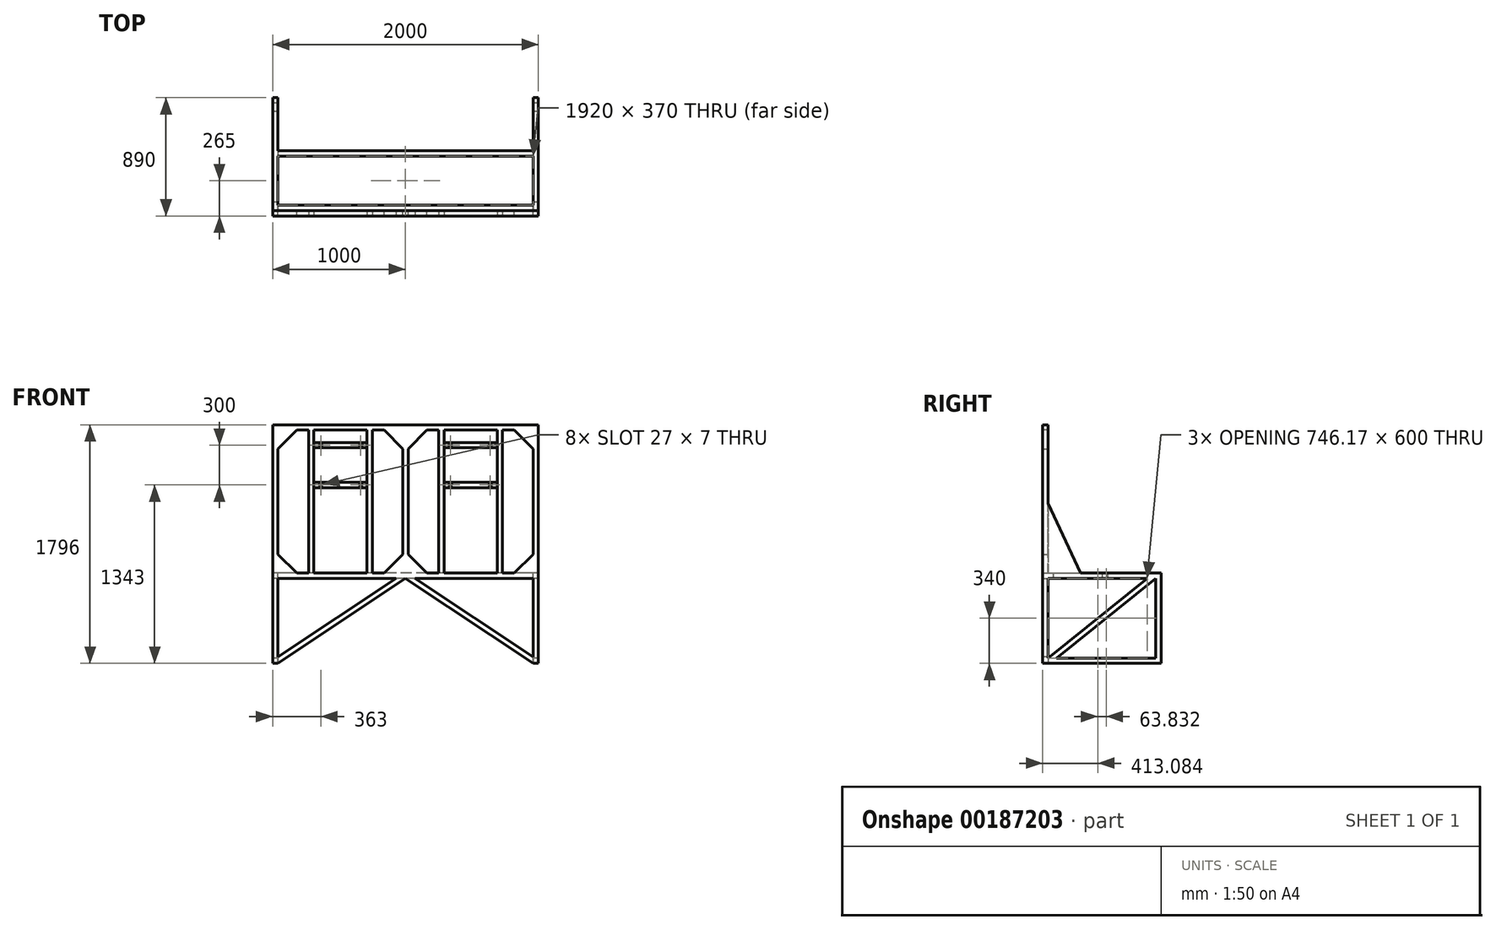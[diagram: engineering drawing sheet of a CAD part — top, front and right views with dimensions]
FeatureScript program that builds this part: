
annotation { "Feature Type Name" : "Feature", "Feature Type Description" : "" }
export const myFeature = defineFeature(function(context is Context, id is Id, definition is map)
    precondition{}
    {
        {
            var Q0;
            Q0=qCreatedBy(makeId("Front.planeOp"),FACE);
            var sketch = newSketch(context, id + "F0", { "sketchPlane" : qUnion([Q0])});
            skLineSegment(sketch, "E0.bottom", {"start": v(1000, -898) * mm, "end": v(-1000, -898) * mm});
            skLineSegment(sketch, "E0.top", {"start": v(1000, 898) * mm, "end": v(-1000, 898) * mm});
            skLineSegment(sketch, "E0.left", {"start": v(1000, -898) * mm, "end": v(1000, 898) * mm});
            skLineSegment(sketch, "E0.right", {"start": v(-1000, -898) * mm, "end": v(-1000, 898) * mm});
            skPoint(sketch, "E0.middle", {"position": v(0, 0) * mm});
            skSolve(sketch);
        }
        {
            var Q0;
            Q0 = qSketchRegion(id + "F0", true);
            extrude(context, id + "F1", {"entities" : qUnion([Q0]), "depth" : 40 * mm});
        }
        {
            var Q0;
            Q0=makeQuery(id+"F1.opExtrude","CAP_FACE",FACE,{"disambiguationData":[OSD([sQuery(id+"F0.wireOp",EDGE,"E0.bottom"),sQuery(id+"F0.wireOp",EDGE,"E0.top"),sQuery(id+"F0.wireOp",EDGE,"E0.left"),sQuery(id+"F0.wireOp",EDGE,"E0.right")])],"isStart":true});
            var sketch = newSketch(context, id + "F2", { "sketchPlane" : qUnion([Q0])});
            skLineSegment(sketch, "E1.bottom", {"start": v(-1000, -218) * mm, "end": v(1000, -218) * mm});
            skLineSegment(sketch, "E1.top", {"start": v(-1000, -898) * mm, "end": v(1000, -898) * mm});
            skLineSegment(sketch, "E1.left", {"start": v(1000, -218) * mm, "end": v(1000, -898) * mm});
            skLineSegment(sketch, "E1.right", {"start": v(-1000, -218) * mm, "end": v(-1000, -898) * mm});
            skSolve(sketch);
        }
        {
            var Q0;
            Q0 = qSketchRegion(id + "F2", true);
            extrude(context, id + "F3", {"entities" : qUnion([Q0]), "operationType" : NewBodyOperationType.ADD, "depth" : 850 * mm});
        }
        {
            var Q0;
            Q0=makeQuery(id+"F1.opExtrude","CAP_FACE",FACE,{"disambiguationData":[OSD([sQuery(id+"F0.wireOp",EDGE,"E0.bottom"),sQuery(id+"F0.wireOp",EDGE,"E0.top"),sQuery(id+"F0.wireOp",EDGE,"E0.left"),sQuery(id+"F0.wireOp",EDGE,"E0.right")])],"isStart":true});
            var sketch = newSketch(context, id + "F4", { "sketchPlane" : qUnion([Q0])});
            skLineSegment(sketch, "E2", {"start": v(0, 898) * mm, "end": v(0, -898) * mm, "construction": true});
            skLineSegment(sketch, "E3.bottom", {"start": v(960, -898) * mm, "end": v(-960, -898) * mm});
            skLineSegment(sketch, "E3.top", {"start": v(960, -258) * mm, "end": v(-960, -258) * mm});
            skLineSegment(sketch, "E3.left", {"start": v(-960, -898) * mm, "end": v(-960, -258) * mm});
            skLineSegment(sketch, "E3.right", {"start": v(960, -898) * mm, "end": v(960, -258) * mm});
            skPoint(sketch, "E3.middle", {"position": v(0, -578) * mm});
            skLineSegment(sketch, "E4", {"start": v(-20, -76.58) * mm, "end": v(-20, 716.58) * mm});
            skLineSegment(sketch, "E5.MirrorCS", {"start": v(-960, 716.58) * mm, "end": v(-960, -76.58) * mm});
            skLineSegment(sketch, "E6.MirrorCS", {"start": v(-960, 716.58) * mm, "end": v(-818.58, 858) * mm});
            skLineSegment(sketch, "E7", {"start": v(-818.58, 858) * mm, "end": v(-161.42, 858) * mm});
            skLineSegment(sketch, "E8", {"start": v(-161.42, 858) * mm, "end": v(-20, 716.58) * mm});
            skLineSegment(sketch, "E9.MirrorCS", {"start": v(20, -76.58) * mm, "end": v(20, 716.58) * mm});
            skLineSegment(sketch, "E10.MirrorCS", {"start": v(960, 716.58) * mm, "end": v(960, -76.58) * mm});
            skLineSegment(sketch, "E11.MirrorCS", {"start": v(960, 716.58) * mm, "end": v(818.58, 858) * mm});
            skLineSegment(sketch, "E12.MirrorCS", {"start": v(818.58, 858) * mm, "end": v(161.42, 858) * mm});
            skLineSegment(sketch, "E13.MirrorCS", {"start": v(161.42, 858) * mm, "end": v(20, 716.58) * mm});
            skLineSegment(sketch, "E14", {"start": v(960, 858) * mm, "end": v(960, 773.15) * mm, "construction": true});
            skLineSegment(sketch, "E15", {"start": v(960, 773.15) * mm, "end": v(875.15, 858) * mm, "construction": true});
            skLineSegment(sketch, "E16", {"start": v(875.15, 858) * mm, "end": v(960, 858) * mm, "construction": true});
            skLineSegment(sketch, "E17", {"start": v(818.58, 858) * mm, "end": v(831.56, 858) * mm, "construction": true});
            skPoint(sketch, "E17.endSnap0", {"position": v(917.57, 858) * mm});
            skLineSegment(sketch, "E18", {"start": v(960, 716.58) * mm, "end": v(960, 745.8) * mm, "construction": true});
            skLineSegment(sketch, "E19", {"start": v(490, 858) * mm, "end": v(490, 680.23) * mm, "construction": true});
            skPoint(sketch, "E19.endSnap0", {"position": v(490, 858) * mm});
            skLineSegment(sketch, "E20.MirrorCS", {"start": v(20, 773.15) * mm, "end": v(104.85, 858) * mm, "construction": true});
            skLineSegment(sketch, "E21.MirrorCS", {"start": v(104.85, 858) * mm, "end": v(20, 858) * mm, "construction": true});
            skPoint(sketch, "E22", {"position": v(960, 815.57) * mm});
            skLineSegment(sketch, "E23.MirrorCS", {"start": v(20, 858) * mm, "end": v(20, 773.15) * mm, "construction": true});
            skLineSegment(sketch, "E24.MirrorCS", {"start": v(-20, 773.15) * mm, "end": v(-104.85, 858) * mm, "construction": true});
            skLineSegment(sketch, "E25.MirrorCS", {"start": v(-20, 858) * mm, "end": v(-20, 773.15) * mm, "construction": true});
            skLineSegment(sketch, "E26.MirrorCS", {"start": v(-104.85, 858) * mm, "end": v(-20, 858) * mm, "construction": true});
            skLineSegment(sketch, "E27.MirrorCS", {"start": v(-960, 773.15) * mm, "end": v(-875.15, 858) * mm, "construction": true});
            skLineSegment(sketch, "E28.MirrorCS", {"start": v(-875.15, 858) * mm, "end": v(-960, 858) * mm, "construction": true});
            skLineSegment(sketch, "E29.MirrorCS", {"start": v(-960, 858) * mm, "end": v(-960, 773.15) * mm, "construction": true});
            skLineSegment(sketch, "E30", {"start": v(-960, -76.58) * mm, "end": v(-818.58, -218) * mm});
            skLineSegment(sketch, "E31", {"start": v(-818.58, -218) * mm, "end": v(-161.42, -218) * mm});
            skLineSegment(sketch, "E32", {"start": v(-161.42, -218) * mm, "end": v(-20, -76.58) * mm});
            skLineSegment(sketch, "E33.MirrorCS", {"start": v(161.42, -218) * mm, "end": v(20, -76.58) * mm});
            skLineSegment(sketch, "E34.MirrorCS", {"start": v(818.58, -218) * mm, "end": v(161.42, -218) * mm});
            skLineSegment(sketch, "E35.MirrorCS", {"start": v(960, -76.58) * mm, "end": v(818.58, -218) * mm});
            skPoint(sketch, "E36.0", {"position": v(1000, -218) * mm});
            skLineSegment(sketch, "E37", {"start": v(1000, -218) * mm, "end": v(818.58, -218) * mm, "construction": true});
            skSolve(sketch);
        }
        {
            var Q0;
            Q0 = qSketchRegion(id + "F4", true);
            extrude(context, id + "F5", {"entities" : qUnion([Q0]), "operationType" : NewBodyOperationType.REMOVE, "endBound" : BoundingType.THROUGH_ALL, "oppositeDirection" : true, "depth" : 25 * mm, "hasSecondDirection" : true, "secondDirectionBound" : SecondDirectionBoundingType.THROUGH_ALL, "secondDirectionOppositeDirection" : false, "secondDirectionDepth" : 25 * mm});
        }
        {
            var Q0;
            Q0=makeQuery(id+"F3.boolean.opBoolean","MERGE",FACE,{"derivedFrom":[makeQuery(id+"F1.opExtrude","SWEPT_FACE",FACE,{"disambiguationData":[OSD([sQuery(id+"F0.wireOp",EDGE,"E0.right")])]}),makeQuery(id+"F3.opExtrude","SWEPT_FACE",FACE,{"disambiguationData":[OSD([sQuery(id+"F2.wireOp",EDGE,"E1.left")])]})]});
            var sketch = newSketch(context, id + "F6", { "sketchPlane" : qUnion([Q0])});
            skLineSegment(sketch, "E38", {"start": v(-810, -258) * mm, "end": v(-810, -858) * mm});
            skLineSegment(sketch, "E39", {"start": v(-810, -858) * mm, "end": v(-63.83, -858) * mm});
            skLineSegment(sketch, "E40", {"start": v(-810, -258) * mm, "end": v(-63.83, -858) * mm});
            skLineSegment(sketch, "E41", {"start": v(0, -258) * mm, "end": v(0, -858) * mm});
            skLineSegment(sketch, "E42", {"start": v(0, -258) * mm, "end": v(-746.17, -258) * mm});
            skLineSegment(sketch, "E43", {"start": v(-746.17, -258) * mm, "end": v(0, -858) * mm});
            skSolve(sketch);
        }
        {
            var Q0;
            Q0 = qSketchRegion(id + "F6", true);
            extrude(context, id + "F7", {"entities" : qUnion([Q0]), "operationType" : NewBodyOperationType.REMOVE, "endBound" : BoundingType.THROUGH_ALL, "oppositeDirection" : true, "depth" : 25 * mm});
        }
        {
            var Q0;
            Q0=makeQuery(id+"F5.boolean.opBoolean","MERGE",FACE,{"derivedFrom":[makeQuery(id+"F3.opExtrude","SWEPT_FACE",FACE,{"disambiguationData":[OSD([sQuery(id+"F2.wireOp",EDGE,"E1.bottom")])]}),makeQuery(id+"F5.opExtrude","SWEPT_FACE",FACE,{"disambiguationData":[OSD([sQuery(id+"F4.wireOp",EDGE,"LeFSMORJ-KBJo-bJ4F-I0GN-BgiXlnm71I2b")])]}),makeQuery(id+"F5.opExtrude","SWEPT_FACE",FACE,{"disambiguationData":[OSD([sQuery(id+"F4.wireOp",EDGE,"b5f1aef8-d078-427e-881c-455c319d67770.MirrorCS")])]})]});
            var sketch = newSketch(context, id + "F8", { "sketchPlane" : qUnion([Q0])});
            skLineSegment(sketch, "E44", {"start": v(0, 900) * mm, "end": v(0, 210.95) * mm, "construction": true});
            skPoint(sketch, "E44.endSnap0", {"position": v(0, 984.2) * mm});
            skLineSegment(sketch, "E45.bottom", {"start": v(960, 450) * mm, "end": v(-960, 450) * mm});
            skLineSegment(sketch, "E45.top", {"start": v(960, 850) * mm, "end": v(-960, 850) * mm});
            skLineSegment(sketch, "E45.left", {"start": v(960, 450) * mm, "end": v(960, 850) * mm});
            skLineSegment(sketch, "E45.right", {"start": v(-960, 450) * mm, "end": v(-960, 850) * mm});
            skPoint(sketch, "E45.middle", {"position": v(0, 650) * mm});
            skLineSegment(sketch, "E46.bottom", {"start": v(960, 40) * mm, "end": v(-960, 40) * mm});
            skLineSegment(sketch, "E46.top", {"start": v(960, 410) * mm, "end": v(-960, 410) * mm});
            skLineSegment(sketch, "E46.left", {"start": v(960, 40) * mm, "end": v(960, 410) * mm});
            skLineSegment(sketch, "E46.right", {"start": v(-960, 40) * mm, "end": v(-960, 410) * mm});
            skPoint(sketch, "E46.middle", {"position": v(0, 225) * mm});
            skSolve(sketch);
        }
        {
            var Q0;
            Q0 = qSketchRegion(id + "F8", true);
            extrude(context, id + "F9", {"entities" : qUnion([Q0]), "operationType" : NewBodyOperationType.REMOVE, "endBound" : BoundingType.THROUGH_ALL, "oppositeDirection" : true, "depth" : 25 * mm});
        }
        {
            var Q0;
            Q0=makeQuery(id+"F1.opExtrude","CAP_FACE",FACE,{"disambiguationData":[OSD([sQuery(id+"F0.wireOp",EDGE,"E0.bottom"),sQuery(id+"F0.wireOp",EDGE,"E0.top"),sQuery(id+"F0.wireOp",EDGE,"E0.left"),sQuery(id+"F0.wireOp",EDGE,"E0.right")])],"isStart":false});
            var sketch = newSketch(context, id + "F10", { "sketchPlane" : qUnion([Q0])});
            skLineSegment(sketch, "E47", {"start": v(0, -258) * mm, "end": v(0, -518.97) * mm, "construction": true});
            skPoint(sketch, "E47.endSnap0", {"position": v(0, -258) * mm});
            skLineSegment(sketch, "E48", {"start": v(0, -258) * mm, "end": v(-960, -898) * mm});
            skLineSegment(sketch, "E49", {"start": v(-72.11, -258) * mm, "end": v(-960, -849.93) * mm});
            skLineSegment(sketch, "E50.MirrorCS", {"start": v(0, -258) * mm, "end": v(960, -898) * mm});
            skLineSegment(sketch, "E51.MirrorCS", {"start": v(72.11, -258) * mm, "end": v(960, -849.93) * mm});
            skLineSegment(sketch, "E52", {"start": v(0, -258) * mm, "end": v(-72.11, -258) * mm});
            skLineSegment(sketch, "E53", {"start": v(-960, -849.93) * mm, "end": v(-960, -898) * mm});
            skLineSegment(sketch, "E54.MirrorCS", {"start": v(960, -849.93) * mm, "end": v(960, -898) * mm});
            skLineSegment(sketch, "E55.MirrorCS", {"start": v(0, -258) * mm, "end": v(72.11, -258) * mm});
            skSolve(sketch);
        }
        {
            var Q0;
            Q0 = qSketchRegion(id + "F10", true);
            extrude(context, id + "F11", {"entities" : qUnion([Q0]), "operationType" : NewBodyOperationType.ADD, "oppositeDirection" : true, "depth" : 40 * mm});
        }
        {
            var Q0;
            Q0=makeQuery(id+"FoXpTRKPhEw7DUg_2.boolean.opBoolean","MERGE",FACE,{"derivedFrom":[makeQuery(id+"FZGJI4E4mUlCNrQ_1.boolean.opBoolean","MERGE",FACE,{"derivedFrom":[makeQuery(id+"F11.boolean.opBoolean","MERGE",FACE,{"derivedFrom":[makeQuery(id+"F1.opExtrude","CAP_FACE",FACE,{"disambiguationData":[OSD([sQuery(id+"F0.wireOp",EDGE,"E0.bottom"),sQuery(id+"F0.wireOp",EDGE,"E0.top"),sQuery(id+"F0.wireOp",EDGE,"E0.left"),sQuery(id+"F0.wireOp",EDGE,"E0.right")])],"isStart":false}),makeQuery(id+"F11.opExtrude","CAP_FACE",FACE,{"disambiguationData":[OSD([sQuery(id+"F10.wireOp",EDGE,"E48"),sQuery(id+"F10.wireOp",EDGE,"E49"),sQuery(id+"F10.wireOp",EDGE,"E52"),sQuery(id+"F10.wireOp",EDGE,"E53")])],"isStart":true}),makeQuery(id+"F11.opExtrude","CAP_FACE",FACE,{"disambiguationData":[OSD([sQuery(id+"F10.wireOp",EDGE,"E50.MirrorCS"),sQuery(id+"F10.wireOp",EDGE,"E51.MirrorCS"),sQuery(id+"F10.wireOp",EDGE,"E54.MirrorCS"),sQuery(id+"F10.wireOp",EDGE,"E55.MirrorCS")])],"isStart":true})]}),makeQuery(id+"FZGJI4E4mUlCNrQ_1.opExtrude","SWEPT_FACE",FACE,{"disambiguationData":[OSD([sQuery(id+"F2cN5tidunm1KXO_1.wireOp",EDGE,"B6aVEywH-Fo3N-waAX-fN73-OkDphfYnpIfc")])]})]}),makeQuery(id+"FoXpTRKPhEw7DUg_2.opExtrude","SWEPT_FACE",FACE,{"disambiguationData":[OSD([sQuery(id+"FMkWsH3aPkv592B_2.wireOp",EDGE,"YWnj1jYQ-A1Ux-tJnZ-8Nos-uWhglmEcxNfV")])]})]});
            var sketch = newSketch(context, id + "F12", { "sketchPlane" : qUnion([Q0])});
            skLineSegment(sketch, "E56.bottom", {"start": v(-730, 858) * mm, "end": v(-690, 858) * mm});
            skLineSegment(sketch, "E56.top", {"start": v(-730, -218) * mm, "end": v(-690, -218) * mm});
            skLineSegment(sketch, "E56.left", {"start": v(-730, 858) * mm, "end": v(-730, -218) * mm});
            skLineSegment(sketch, "E56.right", {"start": v(-690, 858) * mm, "end": v(-690, -218) * mm});
            skLineSegment(sketch, "E57", {"start": v(-490, 858) * mm, "end": v(-490, -218) * mm, "construction": true});
            skLineSegment(sketch, "E58.MirrorCS", {"start": v(-290, 858) * mm, "end": v(-290, -218) * mm});
            skLineSegment(sketch, "E59.MirrorCS", {"start": v(-250, 858) * mm, "end": v(-250, -218) * mm});
            skLineSegment(sketch, "E60.MirrorCS", {"start": v(-250, 858) * mm, "end": v(-290, 858) * mm});
            skLineSegment(sketch, "E61.MirrorCS", {"start": v(-250, -218) * mm, "end": v(-290, -218) * mm});
            skLineSegment(sketch, "E62", {"start": v(0, 898) * mm, "end": v(0, -218) * mm, "construction": true});
            skLineSegment(sketch, "E63.MirrorCS", {"start": v(250, 858) * mm, "end": v(250, -218) * mm});
            skLineSegment(sketch, "E64.MirrorCS", {"start": v(290, 858) * mm, "end": v(290, -218) * mm});
            skLineSegment(sketch, "E65.MirrorCS", {"start": v(690, 858) * mm, "end": v(690, -218) * mm});
            skLineSegment(sketch, "E66.MirrorCS", {"start": v(730, 858) * mm, "end": v(730, -218) * mm});
            skLineSegment(sketch, "E67.MirrorCS", {"start": v(730, -218) * mm, "end": v(690, -218) * mm});
            skLineSegment(sketch, "E68.MirrorCS", {"start": v(250, -218) * mm, "end": v(290, -218) * mm});
            skLineSegment(sketch, "E69.MirrorCS", {"start": v(250, 858) * mm, "end": v(290, 858) * mm});
            skLineSegment(sketch, "E70.MirrorCS", {"start": v(730, 858) * mm, "end": v(690, 858) * mm});
            skLineSegment(sketch, "E71", {"start": v(-161.42, -218) * mm, "end": v(161.42, -218) * mm, "construction": true});
            skSolve(sketch);
        }
        {
            var Q0;
            Q0 = qSketchRegion(id + "F12", true);
            extrude(context, id + "F13", {"entities" : qUnion([Q0]), "operationType" : NewBodyOperationType.ADD, "oppositeDirection" : true, "depth" : 40 * mm});
        }
        {
            var Q0;
            Q0=makeQuery(id+"F13.boolean.opBoolean","MERGE",FACE,{"derivedFrom":[makeQuery(id+"F1.opExtrude","CAP_FACE",FACE,{"disambiguationData":[OSD([sQuery(id+"F0.wireOp",EDGE,"E0.bottom"),sQuery(id+"F0.wireOp",EDGE,"E0.top"),sQuery(id+"F0.wireOp",EDGE,"E0.left"),sQuery(id+"F0.wireOp",EDGE,"E0.right")])],"isStart":true}),makeQuery(id+"F13.opExtrude","CAP_FACE",FACE,{"disambiguationData":[OSD([sQuery(id+"F12.wireOp",EDGE,"E56.bottom"),sQuery(id+"F12.wireOp",EDGE,"E56.top"),sQuery(id+"F12.wireOp",EDGE,"E56.left"),sQuery(id+"F12.wireOp",EDGE,"E56.right")])],"isStart":false}),makeQuery(id+"F13.opExtrude","CAP_FACE",FACE,{"disambiguationData":[OSD([sQuery(id+"F12.wireOp",EDGE,"E58.MirrorCS"),sQuery(id+"F12.wireOp",EDGE,"E59.MirrorCS"),sQuery(id+"F12.wireOp",EDGE,"E60.MirrorCS"),sQuery(id+"F12.wireOp",EDGE,"E61.MirrorCS")])],"isStart":false})]});
            var sketch = newSketch(context, id + "F14", { "sketchPlane" : qUnion([Q0])});
            skLineSegment(sketch, "E72.bottom", {"start": v(690, 765) * mm, "end": v(290, 765) * mm});
            skLineSegment(sketch, "E72.top", {"start": v(690, 725) * mm, "end": v(290, 725) * mm});
            skLineSegment(sketch, "E72.left", {"start": v(690, 765) * mm, "end": v(690, 725) * mm});
            skLineSegment(sketch, "E72.right", {"start": v(290, 765) * mm, "end": v(290, 725) * mm});
            skLineSegment(sketch, "E73", {"start": v(290, 595) * mm, "end": v(690, 595) * mm, "construction": true});
            skLineSegment(sketch, "E74.MirrorCS", {"start": v(290, 425) * mm, "end": v(290, 465) * mm});
            skLineSegment(sketch, "E75.MirrorCS", {"start": v(690, 425) * mm, "end": v(690, 465) * mm});
            skLineSegment(sketch, "E76.MirrorCS", {"start": v(690, 465) * mm, "end": v(290, 465) * mm});
            skLineSegment(sketch, "E77.MirrorCS", {"start": v(690, 425) * mm, "end": v(290, 425) * mm});
            skLineSegment(sketch, "E78", {"start": v(306.58, 745) * mm, "end": v(290, 745) * mm, "construction": true});
            skLineSegment(sketch, "E79", {"start": v(301.9, 445) * mm, "end": v(290, 445) * mm, "construction": true});
            skLineSegment(sketch, "E80", {"start": v(0, 898) * mm, "end": v(0, 53.1) * mm, "construction": true});
            skLineSegment(sketch, "E81.MirrorCS", {"start": v(-690, 725) * mm, "end": v(-290, 725) * mm});
            skLineSegment(sketch, "E82.MirrorCS", {"start": v(-690, 765) * mm, "end": v(-290, 765) * mm});
            skLineSegment(sketch, "E83.MirrorCS", {"start": v(-690, 765) * mm, "end": v(-690, 725) * mm});
            skLineSegment(sketch, "E84.MirrorCS", {"start": v(-290, 765) * mm, "end": v(-290, 725) * mm});
            skLineSegment(sketch, "E85.MirrorCS", {"start": v(-690, 465) * mm, "end": v(-290, 465) * mm});
            skLineSegment(sketch, "E86.MirrorCS", {"start": v(-690, 425) * mm, "end": v(-690, 465) * mm});
            skLineSegment(sketch, "E87.MirrorCS", {"start": v(-690, 425) * mm, "end": v(-290, 425) * mm});
            skLineSegment(sketch, "E88.MirrorCS", {"start": v(-290, 425) * mm, "end": v(-290, 465) * mm});
            skCircle(sketch, "E89", {"center": v(337, 745) * mm, "radius": 3.5 * mm});
            skLineSegment(sketch, "E90", {"start": v(487, 637.16) * mm, "end": v(487, 705.3) * mm, "construction": true});
            skCircle(sketch, "E91.MirrorC", {"center": v(637, 745) * mm, "radius": 3.5 * mm});
            skCircle(sketch, "E92.MirrorC", {"center": v(337, 445) * mm, "radius": 3.5 * mm});
            skCircle(sketch, "E93.MirrorC", {"center": v(637, 445) * mm, "radius": 3.5 * mm});
            skCircle(sketch, "E94.MirrorC", {"center": v(-637, 745) * mm, "radius": 3.5 * mm});
            skCircle(sketch, "E95.MirrorC", {"center": v(-337, 745) * mm, "radius": 3.5 * mm});
            skCircle(sketch, "E96.MirrorC", {"center": v(-337, 445) * mm, "radius": 3.5 * mm});
            skCircle(sketch, "E97.MirrorC", {"center": v(-637, 445) * mm, "radius": 3.5 * mm});
            skLineSegment(sketch, "E98", {"start": v(647, 748.5) * mm, "end": v(627, 748.5) * mm});
            skLineSegment(sketch, "E99", {"start": v(647, 741.5) * mm, "end": v(627, 741.5) * mm});
            skLineSegment(sketch, "E100", {"start": v(637, 748.5) * mm, "end": v(637, 741.5) * mm, "construction": true});
            skArc(sketch, "E101", {"start": v(647, 741.5) * mm, "mid": v(650.5, 745) * mm, "end": v(647, 748.5) * mm});
            skArc(sketch, "E102", {"start": v(627, 748.5) * mm, "mid": v(623.5, 745) * mm, "end": v(627, 741.5) * mm});
            skLineSegment(sketch, "E103", {"start": v(637, 745) * mm, "end": v(603.22, 745) * mm, "construction": true});
            skLineSegment(sketch, "E104.MirrorCS", {"start": v(327, 748.5) * mm, "end": v(347, 748.5) * mm});
            skLineSegment(sketch, "E105.MirrorCS", {"start": v(327, 741.5) * mm, "end": v(347, 741.5) * mm});
            skArc(sketch, "E106.MirrorCS", {"start": v(347, 748.5) * mm, "mid": v(350.5, 745) * mm, "end": v(347, 741.5) * mm});
            skArc(sketch, "E107.MirrorCS", {"start": v(327, 741.5) * mm, "mid": v(323.5, 745) * mm, "end": v(327, 748.5) * mm});
            skLineSegment(sketch, "E108.MirrorCS", {"start": v(647, 441.5) * mm, "end": v(627, 441.5) * mm});
            skLineSegment(sketch, "E109.MirrorCS", {"start": v(647, 448.5) * mm, "end": v(627, 448.5) * mm});
            skArc(sketch, "E110.MirrorCS", {"start": v(627, 441.5) * mm, "mid": v(623.5, 445) * mm, "end": v(627, 448.5) * mm});
            skArc(sketch, "E111.MirrorCS", {"start": v(647, 448.5) * mm, "mid": v(650.5, 445) * mm, "end": v(647, 441.5) * mm});
            skLineSegment(sketch, "E112.MirrorCS", {"start": v(327, 441.5) * mm, "end": v(347, 441.5) * mm});
            skLineSegment(sketch, "E113.MirrorCS", {"start": v(327, 448.5) * mm, "end": v(347, 448.5) * mm});
            skArc(sketch, "E114.MirrorCS", {"start": v(327, 448.5) * mm, "mid": v(323.5, 445) * mm, "end": v(327, 441.5) * mm});
            skArc(sketch, "E115.MirrorCS", {"start": v(347, 441.5) * mm, "mid": v(350.5, 445) * mm, "end": v(347, 448.5) * mm});
            skLineSegment(sketch, "E116.MirrorCS", {"start": v(-647, 748.5) * mm, "end": v(-627, 748.5) * mm});
            skLineSegment(sketch, "E117.MirrorCS", {"start": v(-647, 741.5) * mm, "end": v(-627, 741.5) * mm});
            skArc(sketch, "E118.MirrorCS", {"start": v(-627, 748.5) * mm, "mid": v(-623.5, 745) * mm, "end": v(-627, 741.5) * mm});
            skArc(sketch, "E119.MirrorCS", {"start": v(-647, 741.5) * mm, "mid": v(-650.5, 745) * mm, "end": v(-647, 748.5) * mm});
            skLineSegment(sketch, "E120.MirrorCS", {"start": v(-327, 748.5) * mm, "end": v(-347, 748.5) * mm});
            skLineSegment(sketch, "E121.MirrorCS", {"start": v(-327, 741.5) * mm, "end": v(-347, 741.5) * mm});
            skArc(sketch, "E122.MirrorCS", {"start": v(-327, 741.5) * mm, "mid": v(-323.5, 745) * mm, "end": v(-327, 748.5) * mm});
            skArc(sketch, "E123.MirrorCS", {"start": v(-347, 748.5) * mm, "mid": v(-350.5, 745) * mm, "end": v(-347, 741.5) * mm});
            skLineSegment(sketch, "E124.MirrorCS", {"start": v(-647, 448.5) * mm, "end": v(-627, 448.5) * mm});
            skLineSegment(sketch, "E125.MirrorCS", {"start": v(-647, 441.5) * mm, "end": v(-627, 441.5) * mm});
            skArc(sketch, "E126.MirrorCS", {"start": v(-647, 448.5) * mm, "mid": v(-650.5, 445) * mm, "end": v(-647, 441.5) * mm});
            skArc(sketch, "E127.MirrorCS", {"start": v(-627, 441.5) * mm, "mid": v(-623.5, 445) * mm, "end": v(-627, 448.5) * mm});
            skLineSegment(sketch, "E128.MirrorCS", {"start": v(-327, 448.5) * mm, "end": v(-347, 448.5) * mm});
            skLineSegment(sketch, "E129.MirrorCS", {"start": v(-327, 441.5) * mm, "end": v(-347, 441.5) * mm});
            skArc(sketch, "E130.MirrorCS", {"start": v(-327, 448.5) * mm, "mid": v(-323.5, 445) * mm, "end": v(-327, 441.5) * mm});
            skArc(sketch, "E131.MirrorCS", {"start": v(-347, 441.5) * mm, "mid": v(-350.5, 445) * mm, "end": v(-347, 448.5) * mm});
            skSolve(sketch);
        }
        {
            var Q0;
            Q0 = qSketchRegion(id + "F14", true);
            extrude(context, id + "F15", {"entities" : qUnion([Q0]), "operationType" : NewBodyOperationType.ADD, "oppositeDirection" : true, "depth" : 3 * mm});
        }
        {
            var Q0;
            Q0=makeQuery(id+"F3.boolean.opBoolean","MERGE",FACE,{"derivedFrom":[makeQuery(id+"F1.opExtrude","SWEPT_FACE",FACE,{"disambiguationData":[OSD([sQuery(id+"F0.wireOp",EDGE,"E0.right")])]}),makeQuery(id+"F3.opExtrude","SWEPT_FACE",FACE,{"disambiguationData":[OSD([sQuery(id+"F2.wireOp",EDGE,"E1.left")])]})]});
            var sketch = newSketch(context, id + "F16", { "sketchPlane" : qUnion([Q0])});
            skLineSegment(sketch, "E132", {"start": v(-263.1, -258) * mm, "end": v(40, 392) * mm});
            skLineSegment(sketch, "E133", {"start": v(40, 392) * mm, "end": v(40, -258) * mm});
            skLineSegment(sketch, "E134", {"start": v(40, -258) * mm, "end": v(-263.1, -258) * mm});
            skSolve(sketch);
        }
        {
            var Q0;
            Q0 = qSketchRegion(id + "F16", true);
            extrude(context, id + "F17", {"entities" : qUnion([Q0]), "operationType" : NewBodyOperationType.ADD, "oppositeDirection" : true, "depth" : 2 * mm});
        }
        {
            var Q0;
            Q0=makeQuery(id+"F3.boolean.opBoolean","MERGE",FACE,{"derivedFrom":[makeQuery(id+"F1.opExtrude","SWEPT_FACE",FACE,{"disambiguationData":[OSD([sQuery(id+"F0.wireOp",EDGE,"E0.left")])]}),makeQuery(id+"F3.opExtrude","SWEPT_FACE",FACE,{"disambiguationData":[OSD([sQuery(id+"F2.wireOp",EDGE,"E1.right")])]})]});
            var sketch = newSketch(context, id + "F18", { "sketchPlane" : qUnion([Q0])});
            skLineSegment(sketch, "E135", {"start": v(263.1, -258) * mm, "end": v(-40, -258) * mm});
            skLineSegment(sketch, "E136", {"start": v(-40, -258) * mm, "end": v(-40, 392) * mm});
            skLineSegment(sketch, "E137", {"start": v(-40, 392) * mm, "end": v(263.1, -258) * mm});
            skSolve(sketch);
        }
        {
            var Q0;
            Q0 = qSketchRegion(id + "F18", true);
            extrude(context, id + "F19", {"entities" : qUnion([Q0]), "operationType" : NewBodyOperationType.ADD, "oppositeDirection" : true, "depth" : 2 * mm});
        }
    });
